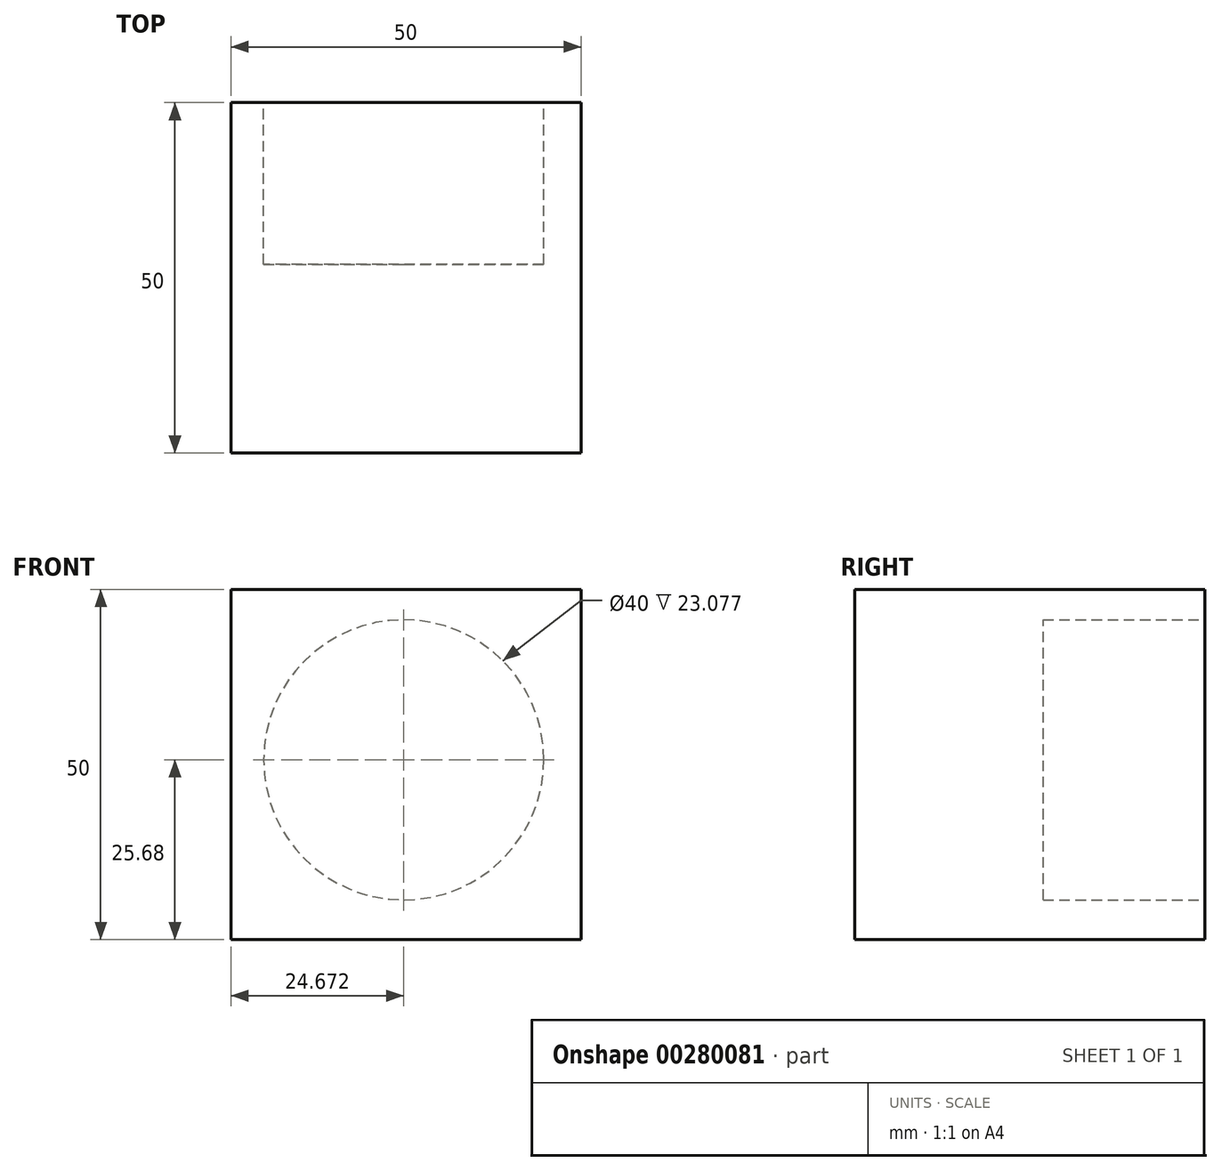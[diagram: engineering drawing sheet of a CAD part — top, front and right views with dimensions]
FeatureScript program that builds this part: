
annotation { "Feature Type Name" : "Feature", "Feature Type Description" : "" }
export const myFeature = defineFeature(function(context is Context, id is Id, definition is map)
    precondition{}
    {
        {
            var Q0;
            Q0=qCreatedBy(makeId("Front.planeOp"),FACE);
            var sketch = newSketch(context, id + "F0", { "sketchPlane" : qUnion([Q0])});
            skLineSegment(sketch, "E0.bottom", {"start": v(0, 0) * mm, "end": v(50, 0) * mm});
            skLineSegment(sketch, "E0.top", {"start": v(0, 50) * mm, "end": v(50, 50) * mm});
            skLineSegment(sketch, "E0.left", {"start": v(0, 0) * mm, "end": v(0, 50) * mm});
            skLineSegment(sketch, "E0.right", {"start": v(50, 0) * mm, "end": v(50, 50) * mm});
            skSolve(sketch);
        }
        {
            var Q0;
            Q0 = qSketchRegion(id + "F0", true);
            extrude(context, id + "F1", {"entities" : qUnion([Q0]), "depth" : 50 * mm});
        }
        {
            var Q0;
            Q0=qCreatedBy(makeId("Front.planeOp"),FACE);
            var sketch = newSketch(context, id + "F2", { "sketchPlane" : qUnion([Q0])});
            skCircle(sketch, "E1", {"center": v(24.67, 25.68) * mm, "radius": 20 * mm});
            skSolve(sketch);
        }
        {
            var Q0;
            Q0=makeQuery(id+"F2.imprint","IMPRINT",FACE,{"disambiguationData":[TD([[makeQuery(id+"F2.imprint","IMPRINT",EDGE,{"derivedFrom":sQuery(id+"F2.wireOp",EDGE,"E1")}),1.0]])]});
            extrude(context, id + "F3", {"entities" : qUnion([Q0]), "operationType" : NewBodyOperationType.REMOVE, "depth" : 23.08 * mm});
        }
    });
